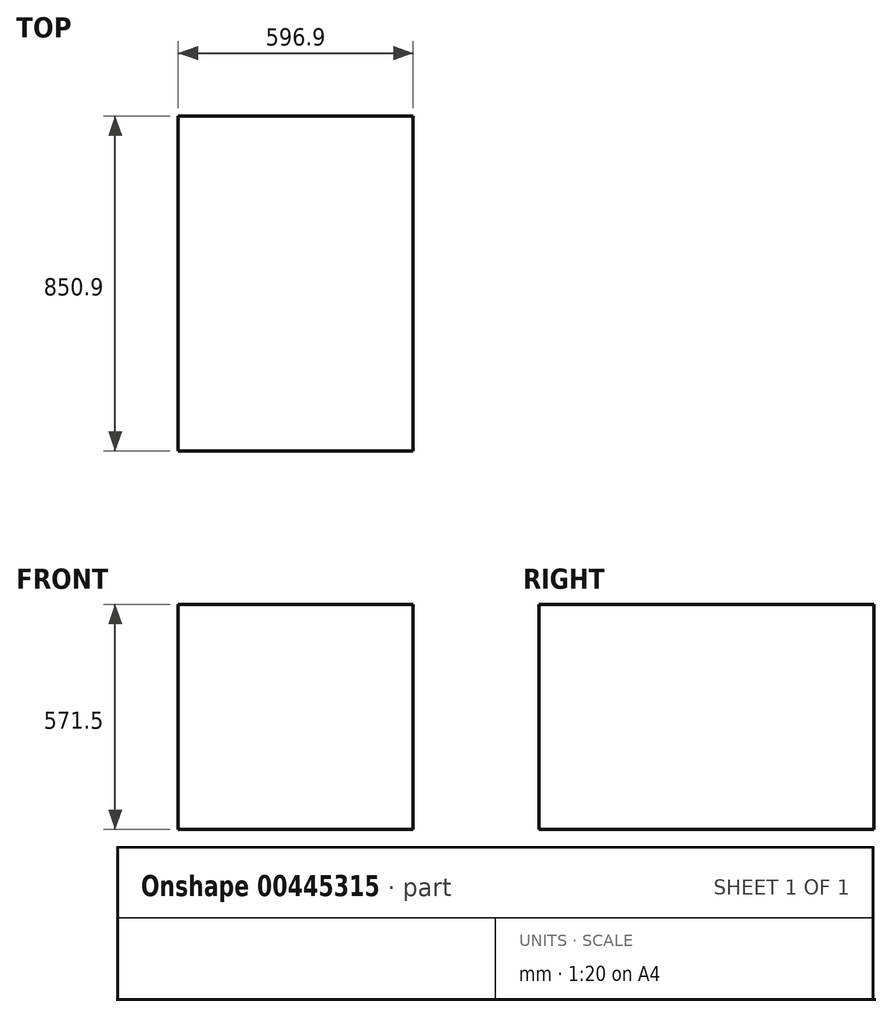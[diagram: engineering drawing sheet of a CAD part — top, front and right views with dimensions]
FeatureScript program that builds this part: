
annotation { "Feature Type Name" : "Feature", "Feature Type Description" : "" }
export const myFeature = defineFeature(function(context is Context, id is Id, definition is map)
    precondition{}
    {
        {
            var Q0;
            Q0=qCreatedBy(makeId("Top.planeOp"),FACE);
            var sketch = newSketch(context, id + "F0", { "sketchPlane" : qUnion([Q0])});
            skLineSegment(sketch, "E0.bottom", {"start": v(0, 0) * mm, "end": v(596.9, 0) * mm});
            skLineSegment(sketch, "E0.top", {"start": v(0, 850.9) * mm, "end": v(596.9, 850.9) * mm});
            skLineSegment(sketch, "E0.left", {"start": v(0, 0) * mm, "end": v(0, 850.9) * mm});
            skLineSegment(sketch, "E0.right", {"start": v(596.9, 0) * mm, "end": v(596.9, 850.9) * mm});
            skSolve(sketch);
        }
        {
            var Q0;
            Q0=makeQuery(id+"F0.imprint","IMPRINT",FACE,{"disambiguationData":[TD([[makeQuery(id+"F0.imprint","IMPRINT",EDGE,{"derivedFrom":sQuery(id+"F0.wireOp",EDGE,"E0.bottom")}),1.0]])]});
            extrude(context, id + "F1", {"entities" : qUnion([Q0]), "depth" : 571.5 * mm});
        }
    });
